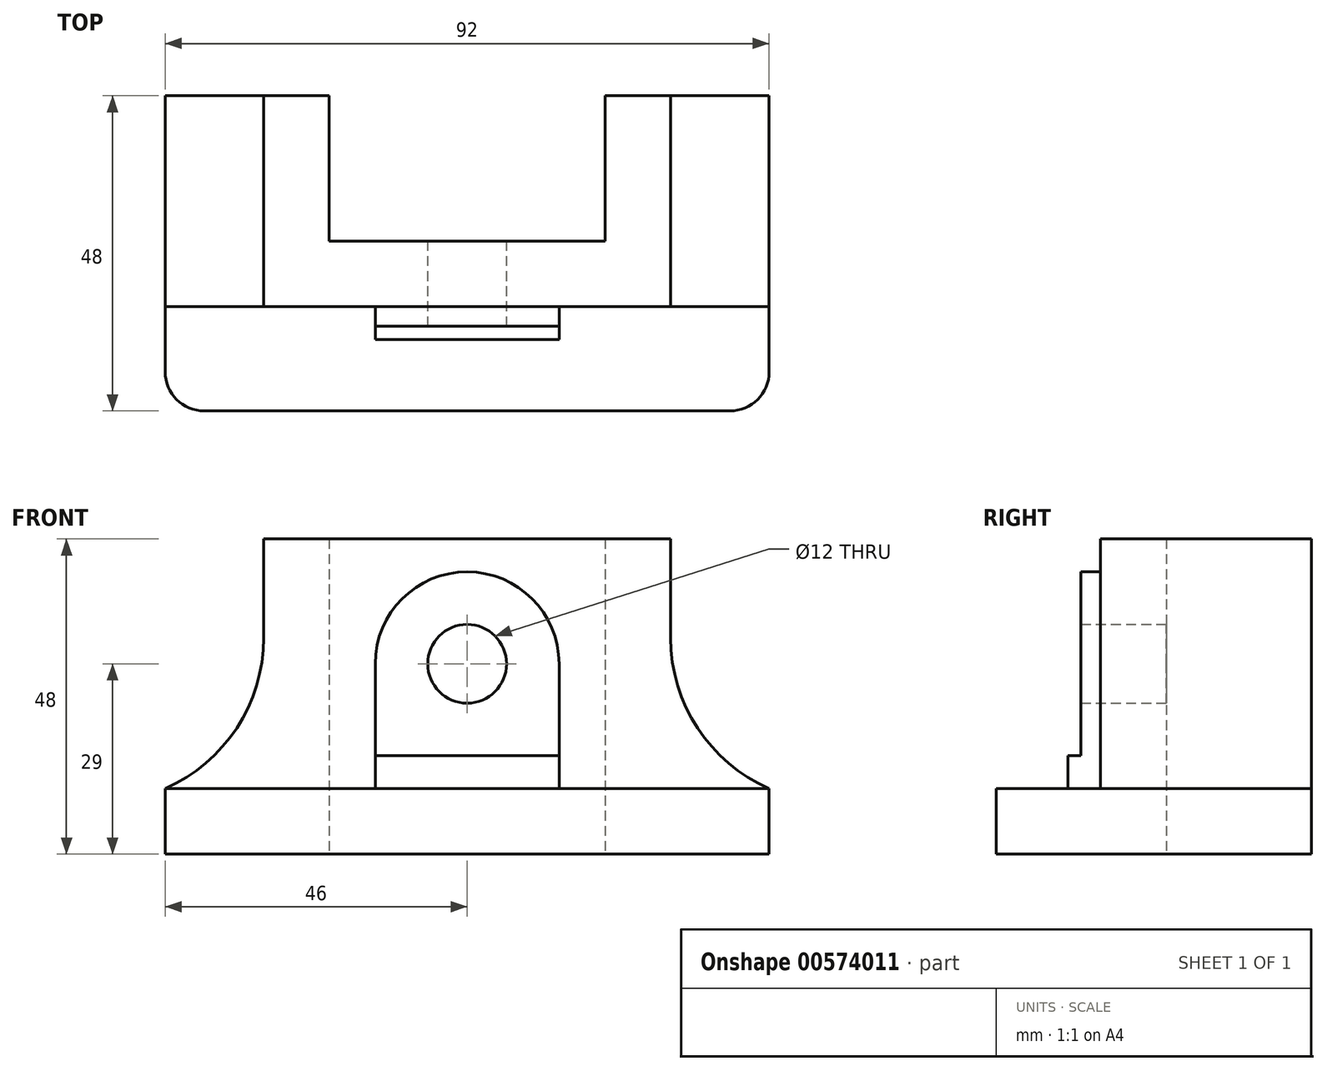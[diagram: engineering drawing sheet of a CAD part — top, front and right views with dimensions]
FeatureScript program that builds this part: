
annotation { "Feature Type Name" : "Feature", "Feature Type Description" : "" }
export const myFeature = defineFeature(function(context is Context, id is Id, definition is map)
    precondition{}
    {
        {
            var Q0;
            Q0=qCreatedBy(makeId("Top.planeOp"),FACE);
            var sketch = newSketch(context, id + "F0", { "sketchPlane" : qUnion([Q0])});
            skLineSegment(sketch, "E0.bottom", {"start": v(40, -24) * mm, "end": v(-40, -24) * mm});
            skLineSegment(sketch, "E0.top", {"start": v(46, 24) * mm, "end": v(21, 24) * mm});
            skLineSegment(sketch, "E0.left", {"start": v(46, -18) * mm, "end": v(46, 24) * mm});
            skLineSegment(sketch, "E0.right", {"start": v(-46, -18) * mm, "end": v(-46, 24) * mm});
            skPoint(sketch, "E0.middle", {"position": v(0, 0) * mm});
            skLineSegment(sketch, "E1", {"start": v(-21, 24) * mm, "end": v(-21, 1.9) * mm});
            skLineSegment(sketch, "E2", {"start": v(-21, 1.9) * mm, "end": v(21, 1.9) * mm});
            skLineSegment(sketch, "E3", {"start": v(21, 1.9) * mm, "end": v(21, 24) * mm});
            skLineSegment(sketch, "E4", {"start": v(-31, 24) * mm, "end": v(-31, -8.1) * mm});
            skLineSegment(sketch, "E5", {"start": v(-31, -8.1) * mm, "end": v(31, -8.1) * mm});
            skLineSegment(sketch, "E6", {"start": v(31, -8.1) * mm, "end": v(31, 24) * mm});
            skLineSegment(sketch, "E7.trimOffspring", {"start": v(-21, 24) * mm, "end": v(-46, 24) * mm});
            skPoint(sketch, "E8.visualSharp", {"position": v(46, -24) * mm});
            skArc(sketch, "E8.filletArc", {"start": v(40, -24) * mm, "mid": v(44.24, -22.24) * mm, "end": v(46, -18) * mm});
            skPoint(sketch, "E9.visualSharp", {"position": v(-46, -24) * mm});
            skArc(sketch, "E9.filletArc", {"start": v(-46, -18) * mm, "mid": v(-44.24, -22.24) * mm, "end": v(-40, -24) * mm});
            skSolve(sketch);
        }
        {
            var Q0;
            {var subQ0=sQuery(id+"F0.wireOp",EDGE,"E1");Q0=makeQuery(id+"F0.imprint","IMPRINT",FACE,{"disambiguationData":[TD([[makeQuery(id+"F0.imprint","IMPRINT",EDGE,{"derivedFrom":subQ0}),-1.0]])]});}
            extrude(context, id + "F1", {"entities" : qUnion([Q0]), "depth" : 48 * mm, "offsetDistance" : 25 * mm});
        }
        {
            var Q0;
            Q0 = qSketchRegion(id + "F0", true);
            extrude(context, id + "F2", {"entities" : qUnion([Q0]), "operationType" : NewBodyOperationType.ADD, "depth" : 10 * mm, "offsetDistance" : 25 * mm});
        }
        {
            var Q0;
            Q0=makeQuery(id+"F2.boolean.opBoolean","INTERSECT",EDGE,{"derivedFrom":[makeQuery(id+"F1.opExtrude","SWEPT_FACE",FACE,{"disambiguationData":[OSD([sQuery(id+"F0.wireOp",EDGE,"E6")])]}),makeQuery(id+"F2.opExtrude","CAP_FACE",FACE,{"disambiguationData":[OSD([sQuery(id+"F0.wireOp",EDGE,"E0.bottom"),sQuery(id+"F0.wireOp",EDGE,"E0.top"),sQuery(id+"F0.wireOp",EDGE,"E0.left"),sQuery(id+"F0.wireOp",EDGE,"E0.right"),sQuery(id+"F0.wireOp",EDGE,"E1"),sQuery(id+"F0.wireOp",EDGE,"E2"),sQuery(id+"F0.wireOp",EDGE,"E3"),sQuery(id+"F0.wireOp",EDGE,"E7.trimOffspring"),sQuery(id+"F0.wireOp",EDGE,"E8.filletArc"),sQuery(id+"F0.wireOp",EDGE,"E9.filletArc")])],"isStart":false})]});
            fillet(context, id + "F3", {"entities" : qUnion([Q0]), "radius" : 25 * mm, "tangentPropagation" : true, "allowEdgeOverflow" : false});
        }
        {
            var Q0;
            Q0=makeQuery(id+"F2.boolean.opBoolean","INTERSECT",EDGE,{"derivedFrom":[makeQuery(id+"F1.opExtrude","SWEPT_FACE",FACE,{"disambiguationData":[OSD([sQuery(id+"F0.wireOp",EDGE,"E4")])]}),makeQuery(id+"F2.opExtrude","CAP_FACE",FACE,{"disambiguationData":[OSD([sQuery(id+"F0.wireOp",EDGE,"E0.bottom"),sQuery(id+"F0.wireOp",EDGE,"E0.top"),sQuery(id+"F0.wireOp",EDGE,"E0.left"),sQuery(id+"F0.wireOp",EDGE,"E0.right"),sQuery(id+"F0.wireOp",EDGE,"E1"),sQuery(id+"F0.wireOp",EDGE,"E2"),sQuery(id+"F0.wireOp",EDGE,"E3"),sQuery(id+"F0.wireOp",EDGE,"E7.trimOffspring"),sQuery(id+"F0.wireOp",EDGE,"E8.filletArc"),sQuery(id+"F0.wireOp",EDGE,"E9.filletArc")])],"isStart":false})]});
            fillet(context, id + "F4", {"entities" : qUnion([Q0]), "radius" : 25 * mm, "tangentPropagation" : true, "allowEdgeOverflow" : false});
        }
        {
            var Q0;
            Q0=makeQuery(id+"F1.opExtrude","SWEPT_FACE",FACE,{"disambiguationData":[OSD([sQuery(id+"F0.wireOp",EDGE,"E5")])]});
            var sketch = newSketch(context, id + "F5", { "sketchPlane" : qUnion([Q0])});
            skArc(sketch, "E10", {"start": v(14, 29) * mm, "mid": v(0, 43) * mm, "end": v(-14, 29) * mm});
            skCircle(sketch, "E11", {"center": v(0, 29) * mm, "radius": 6 * mm});
            skLineSegment(sketch, "E12", {"start": v(-14, 29) * mm, "end": v(-14, 10) * mm});
            skLineSegment(sketch, "E13", {"start": v(14, 29) * mm, "end": v(14, 10) * mm});
            skLineSegment(sketch, "E14", {"start": v(-14, 15) * mm, "end": v(14, 15) * mm});
            skSolve(sketch);
        }
        {
            var Q0;
            {var subQ3=sQuery(id+"F5.wireOp",EDGE,"E14");Q0=makeQuery(id+"F5.imprint","IMPRINT",FACE,{"disambiguationData":[TD([[makeQuery(id+"F5.imprint","IMPRINT",EDGE,{"derivedFrom":subQ3}),-1.0]])]});}
            extrude(context, id + "F6", {"entities" : qUnion([Q0]), "operationType" : NewBodyOperationType.ADD, "depth" : 5 * mm, "offsetDistance" : 25 * mm});
        }
        {
            var Q0;
            Q0 = qSketchRegion(id + "F5", true);
            extrude(context, id + "F7", {"entities" : qUnion([Q0]), "operationType" : NewBodyOperationType.ADD, "depth" : 3 * mm, "offsetDistance" : 25 * mm});
        }
        {
            var Q0;
            Q0=makeQuery(id+"F7.boolean.opBoolean","SPLIT",FACE,{"disambiguationData":[TD([makeQuery(id+"F7.opExtrude","SWEPT_FACE",FACE,{"disambiguationData":[OSD([sQuery(id+"F5.wireOp",EDGE,"E11")])]})])],"derivedFrom":makeQuery(id+"F1.opExtrude","SWEPT_FACE",FACE,{"disambiguationData":[OSD([sQuery(id+"F0.wireOp",EDGE,"E5")])]})});
            extrude(context, id + "F8", {"entities" : qUnion([Q0]), "operationType" : NewBodyOperationType.REMOVE, "oppositeDirection" : true, "depth" : 25 * mm, "offsetDistance" : 25 * mm});
        }
    });
